# Revit family: QF_MACOM_RHB2_G_x
name_source: partatom
category: Equipamento especial
units: mm (PartAtom-declared; Revit-internal decimal feet)

## family parameters
Com base no plano de trabalho = Não
Compartilhado = Não
Corte com vazios quando carregada = Não
Cota do conector redondo = Utilizar diâmetro
Número OmniClass = 23.40.40.11.11.11
Ponto de cálculo do ambiente = Não
Sempre na vertical = Sim
Tipo de parte = Normal
Título OmniClass = Refrigerators

## types (2) — shared parameters
Capacity = 190,00 L
Climate Class = 5
Coolant = R134a
Descrição = REFRIGERADOR HORIZONTAL COMERCIAL DE BASE MACOM 2 PORTAS, 12 TRILHOS, 2 PRATELEIRAS PERFURADAS, TAMPO DE CENTRO SERIE 900-1440X800X630
Direct Waste = 1"
Electric Current = 2 A
Electric Power = 329 W
Elevação padrão = 0 mm
Fabricante = MACOM
Height = 630 mm
Lenght = 800 mm
Line Frequency = 60 Hz
Protection Class = IP 22
Show Clearances = Sim
Show Logo = Sim
URL = https://www.acosmacom.com.br
Volts = 220 V
Weight = 116,00 kg
Width = 1440 mm
Work Temperature = 1°C a 10°C

## per-type parameters (varying)
| type | Cover G-7 | Suport | Suport Cover | Volume |
| RHB2-G-9 | Não | Não | Sim | 0,72 m³ |
| RHB2-G-7 | Sim | Sim | Não | 0,63 m³ |

note: column(s) folded — value = type name in every type: Modelo

## geometry (parser evidence)
native form markers: Sweep x18
no freeform markers — native parametric forms only
